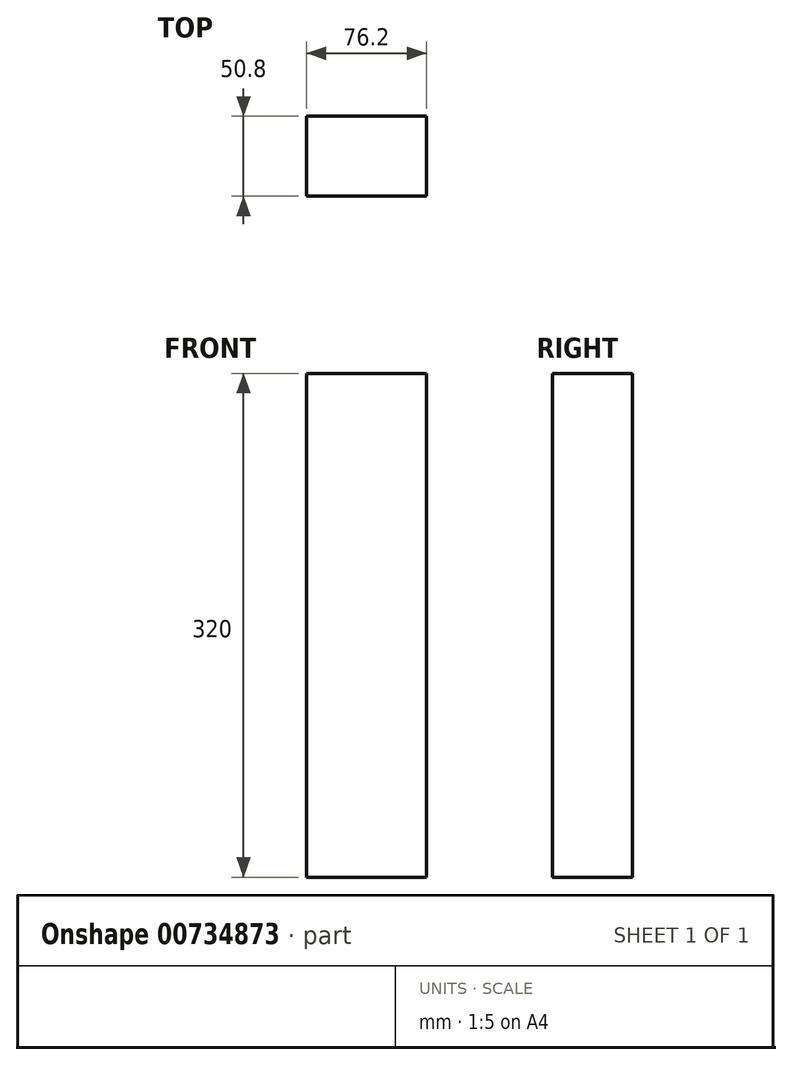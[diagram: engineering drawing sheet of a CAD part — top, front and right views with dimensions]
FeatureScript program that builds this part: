
annotation { "Feature Type Name" : "Feature", "Feature Type Description" : "" }
export const myFeature = defineFeature(function(context is Context, id is Id, definition is map)
    precondition{}
    {
        {
            var Q0;
            Q0=qCreatedBy(makeId("Front.planeOp"),FACE);
            var sketch = newSketch(context, id + "F0", { "sketchPlane" : qUnion([Q0])});
            skLineSegment(sketch, "E0.bottom", {"start": v(-38.1, 160) * mm, "end": v(38.1, 160) * mm});
            skLineSegment(sketch, "E0.top", {"start": v(-38.1, -160) * mm, "end": v(38.1, -160) * mm});
            skLineSegment(sketch, "E0.left", {"start": v(-38.1, 160) * mm, "end": v(-38.1, -160) * mm});
            skLineSegment(sketch, "E0.right", {"start": v(38.1, 160) * mm, "end": v(38.1, -160) * mm});
            skPoint(sketch, "E0.middle", {"position": v(0, 0) * mm});
            skSolve(sketch);
        }
        {
            var Q0;
            Q0=makeQuery(id+"F0.imprint","IMPRINT",FACE,{"disambiguationData":[TD([[makeQuery(id+"F0.imprint","IMPRINT",EDGE,{"derivedFrom":sQuery(id+"F0.wireOp",EDGE,"E0.bottom")}),-1.0]])]});
            extrude(context, id + "F1", {"entities" : qUnion([Q0]), "endBound" : BoundingType.SYMMETRIC, "depth" : 50.8 * mm, "offsetDistance" : 25.4 * mm});
        }
    });
